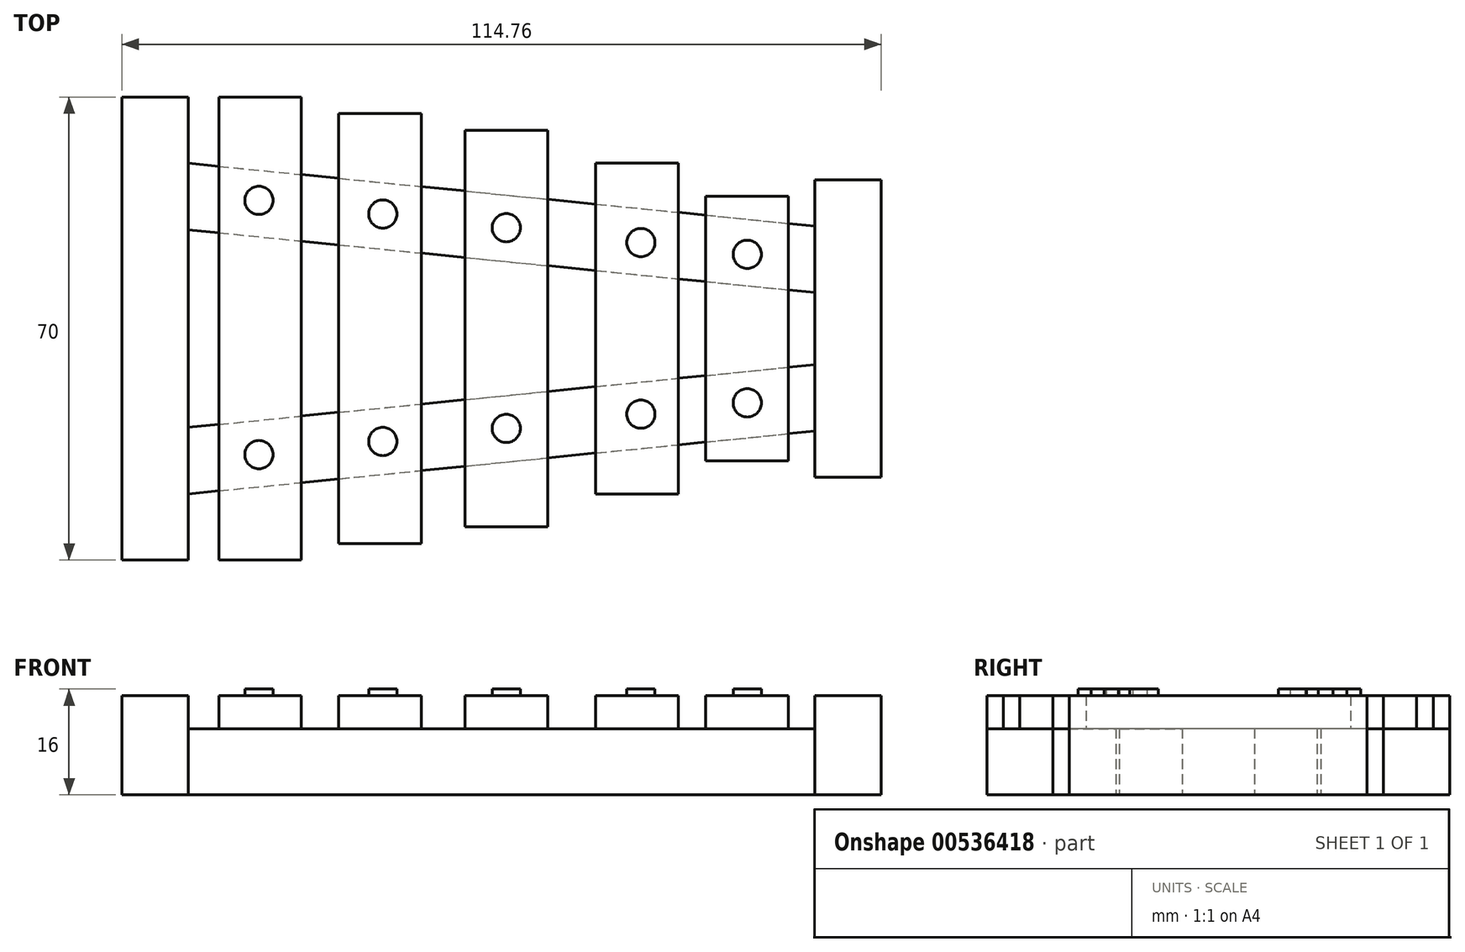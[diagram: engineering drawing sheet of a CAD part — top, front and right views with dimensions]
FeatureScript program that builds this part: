
annotation { "Feature Type Name" : "Feature", "Feature Type Description" : "" }
export const myFeature = defineFeature(function(context is Context, id is Id, definition is map)
    precondition{}
    {
        {
            var Q0;
            Q0=qCreatedBy(makeId("Top.planeOp"),FACE);
            var sketch = newSketch(context, id + "F0", { "sketchPlane" : qUnion([Q0])});
            skLineSegment(sketch, "E0.bottom", {"start": v(-54.7, 35) * mm, "end": v(-44.7, 35) * mm});
            skLineSegment(sketch, "E0.top", {"start": v(-54.7, -35) * mm, "end": v(-44.7, -35) * mm});
            skLineSegment(sketch, "E0.left", {"start": v(-54.7, 35) * mm, "end": v(-54.7, -35) * mm});
            skLineSegment(sketch, "E0.right", {"start": v(-44.7, 35) * mm, "end": v(-44.7, -35) * mm});
            skLineSegment(sketch, "E1.bottom", {"start": v(50.07, 22.5) * mm, "end": v(60.07, 22.5) * mm});
            skLineSegment(sketch, "E1.top", {"start": v(50.07, -22.5) * mm, "end": v(60.07, -22.5) * mm});
            skLineSegment(sketch, "E1.left", {"start": v(50.07, 22.5) * mm, "end": v(50.07, -22.5) * mm});
            skLineSegment(sketch, "E1.right", {"start": v(60.07, 22.5) * mm, "end": v(60.07, -22.5) * mm});
            skLineSegment(sketch, "E2", {"start": v(-44.7, 25) * mm, "end": v(50.07, 15.5) * mm});
            skLineSegment(sketch, "E3", {"start": v(-44.7, 14.95) * mm, "end": v(50.07, 5.45) * mm});
            skLineSegment(sketch, "E4", {"start": v(-44.7, -14.95) * mm, "end": v(50.07, -5.45) * mm});
            skLineSegment(sketch, "E5", {"start": v(-44.7, -25) * mm, "end": v(50.07, -15.5) * mm});
            skSolve(sketch);
        }
        {
            var Q0;
            Q0 = qSketchRegion(id + "F0", true);
            extrude(context, id + "F1", {"entities" : qUnion([Q0]), "depth" : 15 * mm, "offsetDistance" : 25 * mm});
        }
        {
            var Q0;
            Q0=makeQuery(id+"F1.opExtrude","CAP_FACE",FACE,{"disambiguationData":[OSD([sQuery(id+"F0.wireOp",EDGE,"E0.bottom"),sQuery(id+"F0.wireOp",EDGE,"E0.top"),sQuery(id+"F0.wireOp",EDGE,"E0.left"),sQuery(id+"F0.wireOp",EDGE,"E0.right"),sQuery(id+"F0.wireOp",EDGE,"E1.bottom"),sQuery(id+"F0.wireOp",EDGE,"E1.top"),sQuery(id+"F0.wireOp",EDGE,"E1.left"),sQuery(id+"F0.wireOp",EDGE,"E1.right"),sQuery(id+"F0.wireOp",EDGE,"E2"),sQuery(id+"F0.wireOp",EDGE,"E3"),sQuery(id+"F0.wireOp",EDGE,"E4"),sQuery(id+"F0.wireOp",EDGE,"E5")])],"isStart":false});
            var sketch = newSketch(context, id + "F2", { "sketchPlane" : qUnion([Q0])});
            skLineSegment(sketch, "E6.bottom", {"start": v(-44.7, 30) * mm, "end": v(50.07, 30) * mm});
            skLineSegment(sketch, "E6.top", {"start": v(-44.7, -32.22) * mm, "end": v(50.07, -32.22) * mm});
            skLineSegment(sketch, "E6.left", {"start": v(-44.7, 30) * mm, "end": v(-44.7, -32.22) * mm});
            skLineSegment(sketch, "E6.right", {"start": v(50.07, 30) * mm, "end": v(50.07, -32.22) * mm});
            skSolve(sketch);
        }
        {
            var Q0;
            {var subQ4=sQuery(id+"F2.wireOp",EDGE,"E6.bottom");Q0=makeQuery(id+"F2.imprint","IMPRINT",FACE,{"disambiguationData":[TD([[makeQuery(id+"F2.imprint","IMPRINT",EDGE,{"derivedFrom":subQ4}),-1.0]])]});}
            var Q1;
            {var subQ1=makeQuery(id+"F1.opExtrude","CAP_EDGE",EDGE,{"disambiguationData":[OSD([sQuery(id+"F0.wireOp",EDGE,"E2")])],"isStart":false});Q1=makeQuery(id+"F2.imprint","IMPRINT",FACE,{"disambiguationData":[TD([[makeQuery(id+"F2.imprint","IMPRINT",EDGE,{"derivedFrom":subQ1}),-1.0]])]});}
            var Q2;
            {var subQ1=makeQuery(id+"F1.opExtrude","CAP_EDGE",EDGE,{"disambiguationData":[OSD([sQuery(id+"F0.wireOp",EDGE,"E3")])],"isStart":false});Q2=makeQuery(id+"F2.imprint","IMPRINT",FACE,{"disambiguationData":[TD([[makeQuery(id+"F2.imprint","IMPRINT",EDGE,{"derivedFrom":subQ1}),-1.0]])]});}
            var Q3;
            {var subQ1=makeQuery(id+"F1.opExtrude","CAP_EDGE",EDGE,{"disambiguationData":[OSD([sQuery(id+"F0.wireOp",EDGE,"E4")])],"isStart":false});Q3=makeQuery(id+"F2.imprint","IMPRINT",FACE,{"disambiguationData":[TD([[makeQuery(id+"F2.imprint","IMPRINT",EDGE,{"derivedFrom":subQ1}),-1.0]])]});}
            var Q4;
            {var subQ2=sQuery(id+"F2.wireOp",EDGE,"E6.top");Q4=makeQuery(id+"F2.imprint","IMPRINT",FACE,{"disambiguationData":[TD([[makeQuery(id+"F2.imprint","IMPRINT",EDGE,{"derivedFrom":subQ2}),1.0]])]});}
            extrude(context, id + "F3", {"entities" : qUnion([Q0, Q1, Q2, Q3, Q4]), "operationType" : NewBodyOperationType.REMOVE, "oppositeDirection" : true, "depth" : 5 * mm, "offsetDistance" : 25 * mm});
        }
        {
            var Q0;
            {var subQ4=sQuery(id+"F2.wireOp",EDGE,"E6.right");var subQ6=sQuery(id+"F0.wireOp",EDGE,"E2");var subQ7=sQuery(id+"F2.wireOp",EDGE,"E6.left");Q0=makeQuery(id+"F3.boolean.opBoolean","COPY",FACE,{"disambiguationData":[TD([makeQuery(id+"F1.opExtrude","SWEPT_FACE",FACE,{"disambiguationData":[OSD([subQ6])]})])],"derivedFrom":makeQuery(id+"F3.opExtrude","CAP_FACE",FACE,{"disambiguationData":[OSD([sQuery(id+"F2.wireOp",EDGE,"E6.bottom"),sQuery(id+"F2.wireOp",EDGE,"E6.top"),subQ7,subQ4])],"isStart":false})});}
            var sketch = newSketch(context, id + "F4", { "sketchPlane" : qUnion([Q0])});
            skLineSegment(sketch, "E7.bottom", {"start": v(-40.07, 35) * mm, "end": v(-27.57, 35) * mm});
            skLineSegment(sketch, "E7.top", {"start": v(-40.07, -35) * mm, "end": v(-27.57, -35) * mm});
            skLineSegment(sketch, "E7.left", {"start": v(-40.07, 35) * mm, "end": v(-40.07, -35) * mm});
            skLineSegment(sketch, "E7.right", {"start": v(-27.57, 35) * mm, "end": v(-27.57, -35) * mm});
            skLineSegment(sketch, "E8.bottom", {"start": v(-21.92, 32.5) * mm, "end": v(-9.42, 32.5) * mm});
            skLineSegment(sketch, "E8.top", {"start": v(-21.92, -32.5) * mm, "end": v(-9.42, -32.5) * mm});
            skLineSegment(sketch, "E8.left", {"start": v(-21.92, 32.5) * mm, "end": v(-21.92, -32.5) * mm});
            skLineSegment(sketch, "E8.right", {"start": v(-9.42, 32.5) * mm, "end": v(-9.42, -32.5) * mm});
            skLineSegment(sketch, "E9.bottom", {"start": v(16.92, 25) * mm, "end": v(29.42, 25) * mm});
            skLineSegment(sketch, "E9.top", {"start": v(16.92, -25) * mm, "end": v(29.42, -25) * mm});
            skLineSegment(sketch, "E9.left", {"start": v(16.92, 25) * mm, "end": v(16.92, -25) * mm});
            skLineSegment(sketch, "E9.right", {"start": v(29.42, 25) * mm, "end": v(29.42, -25) * mm});
            skLineSegment(sketch, "E10.bottom", {"start": v(33.56, 20) * mm, "end": v(46.06, 20) * mm});
            skLineSegment(sketch, "E10.top", {"start": v(33.56, -20) * mm, "end": v(46.06, -20) * mm});
            skLineSegment(sketch, "E10.left", {"start": v(33.56, 20) * mm, "end": v(33.56, -20) * mm});
            skLineSegment(sketch, "E10.right", {"start": v(46.06, 20) * mm, "end": v(46.06, -20) * mm});
            skLineSegment(sketch, "E11.bottom", {"start": v(-2.8, 30) * mm, "end": v(9.7, 30) * mm});
            skLineSegment(sketch, "E11.top", {"start": v(-2.8, -30) * mm, "end": v(9.7, -30) * mm});
            skLineSegment(sketch, "E11.left", {"start": v(-2.8, 30) * mm, "end": v(-2.8, -30) * mm});
            skLineSegment(sketch, "E11.right", {"start": v(9.7, 30) * mm, "end": v(9.7, -30) * mm});
            skSolve(sketch);
        }
        {
            var Q0;
            Q0 = qSketchRegion(id + "F4", true);
            extrude(context, id + "F5", {"entities" : qUnion([Q0]), "depth" : 5 * mm, "offsetDistance" : 25 * mm});
        }
        {
            var Q0;
            Q0=makeQuery(id+"F5.opExtrude","CAP_FACE",FACE,{"disambiguationData":[OSD([sQuery(id+"F4.wireOp",EDGE,"E7.bottom"),sQuery(id+"F4.wireOp",EDGE,"E7.top"),sQuery(id+"F4.wireOp",EDGE,"E7.left"),sQuery(id+"F4.wireOp",EDGE,"E7.right")])],"isStart":false});
            var sketch = newSketch(context, id + "F6", { "sketchPlane" : qUnion([Q0])});
            skLineSegment(sketch, "E12", {"start": v(-44.69, 20.56) * mm, "end": v(49.9, 10.1) * mm, "construction": true});
            skLineSegment(sketch, "E13", {"start": v(49.9, 10.1) * mm, "end": v(49.9, -10.17) * mm, "construction": true});
            skLineSegment(sketch, "E14", {"start": v(49.9, -10.17) * mm, "end": v(-44.69, -20.2) * mm, "construction": true});
            skCircle(sketch, "E15", {"center": v(-34, 19.38) * mm, "radius": 2.14 * mm});
            skCircle(sketch, "E16", {"center": v(-15.26, 17.3) * mm, "radius": 2.14 * mm});
            skCircle(sketch, "E17", {"center": v(23.76, 13) * mm, "radius": 2.14 * mm});
            skCircle(sketch, "E18", {"center": v(39.85, 11.21) * mm, "radius": 2.14 * mm});
            skCircle(sketch, "E19", {"center": v(3.41, 15.24) * mm, "radius": 2.14 * mm});
            skCircle(sketch, "E20", {"center": v(-34, -19.06) * mm, "radius": 2.14 * mm});
            skCircle(sketch, "E21", {"center": v(-15.26, -17.07) * mm, "radius": 2.14 * mm});
            skCircle(sketch, "E22", {"center": v(3.41, -15.1) * mm, "radius": 2.14 * mm});
            skCircle(sketch, "E23", {"center": v(23.76, -12.94) * mm, "radius": 2.14 * mm});
            skCircle(sketch, "E24", {"center": v(39.85, -11.23) * mm, "radius": 2.14 * mm});
            skSolve(sketch);
        }
        {
            var Q0;
            Q0 = qSketchRegion(id + "F6", true);
            extrude(context, id + "F7", {"entities" : qUnion([Q0]), "depth" : 1 * mm, "offsetDistance" : 25 * mm});
        }
    });
